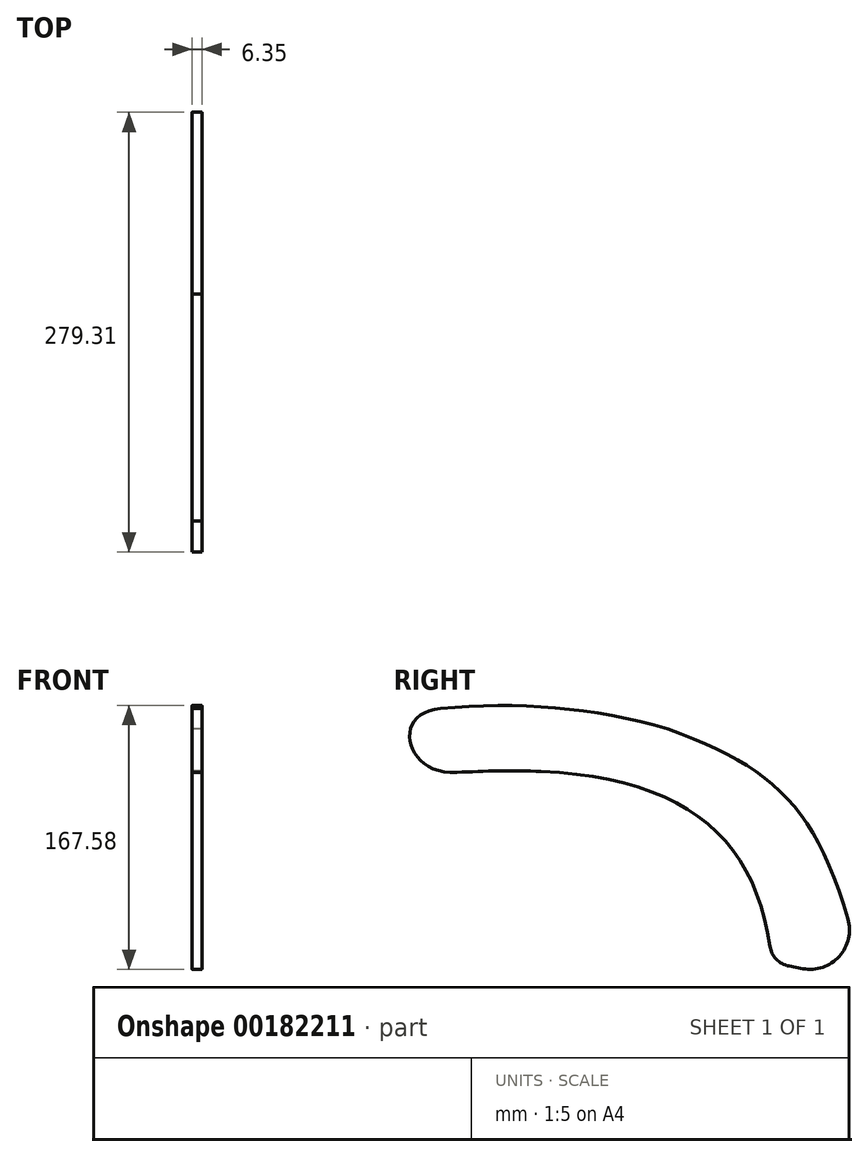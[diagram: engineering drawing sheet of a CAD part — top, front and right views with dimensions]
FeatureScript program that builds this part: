
annotation { "Feature Type Name" : "Feature", "Feature Type Description" : "" }
export const myFeature = defineFeature(function(context is Context, id is Id, definition is map)
    precondition{}
    {
        {
            var Q0;
            Q0=qCreatedBy(makeId("Right.planeOp"),FACE);
            var sketch = newSketch(context, id + "F0", { "sketchPlane" : qUnion([Q0])});
            skFitSpline(sketch, "E0", {"points": [v(0, 0) * mm, v(192, -41) * mm], "startDerivative": vector(239.03, 12.63) * mm, "endDerivative": vector(177.27, -126.97) * mm, "construction": true});
            skArc(sketch, "E1.0.startCap", {"start": v(0.4, -7.49) * mm, "mid": v(-7.49, -0.4) * mm, "end": v(-0.4, 7.49) * mm});
            skArc(sketch, "E1.0.endCap", {"start": v(196.37, -34.9) * mm, "mid": v(198.1, -45.37) * mm, "end": v(187.63, -47.1) * mm});
            skFitSpline(sketch, "E1.0.left", {"points": [v(-0.38, 7.24) * mm, v(19.62, 8.3) * mm, v(47.27, 9.22) * mm, v(81.02, 7.57) * mm, v(105.14, 4.47) * mm, v(128.41, -0.91) * mm, v(151.15, -8.97) * mm, v(173.62, -20.05) * mm, v(188.64, -29.68) * mm, v(196.22, -35.1) * mm]});
            skFitSpline(sketch, "E1.0.right", {"points": [v(0.38, -7.24) * mm, v(20.22, -6.2) * mm, v(47.37, -5.3) * mm, v(79.8, -6.9) * mm, v(102.62, -9.84) * mm, v(124.36, -14.87) * mm, v(145.48, -22.35) * mm, v(166.43, -32.67) * mm, v(180.59, -41.74) * mm, v(187.78, -46.9) * mm]});
            skLineSegment(sketch, "E2", {"start": v(229.1, -144.67) * mm, "end": v(220.28, -143.03) * mm});
            skFitSpline(sketch, "E3", {"points": [v(209.4, -141) * mm, v(62.86, -19.41) * mm], "startDerivative": vector(-20.35, 227.9) * mm, "endDerivative": vector(-284.66, 11.89) * mm});
            skFitSpline(sketch, "E4", {"points": [v(143.32, 7.74) * mm, v(267.73, -151.85) * mm], "startDerivative": vector(228.79, -86.1) * mm, "endDerivative": vector(73.25, -316.4) * mm});
            skArc(sketch, "E5.filletArc", {"start": v(208.17, -130.4) * mm, "mid": v(212.2, -138.66) * mm, "end": v(220.28, -143.03) * mm});
            skArc(sketch, "E6.filletArc", {"start": v(229.1, -144.67) * mm, "mid": v(252.25, -136.83) * mm, "end": v(257.65, -113) * mm});
            skFitSpline(sketch, "E7", {"points": [v(9.37, -20.06) * mm, v(-1.08, 20.47) * mm], "startDerivative": vector(-100.53, -5.96) * mm, "endDerivative": vector(93.66, 6.16) * mm});
            skFitSpline(sketch, "E8", {"points": [v(1.08, -20.47) * mm, v(10.92, -19.95) * mm, v(29.66, -19.14) * mm, v(55.26, -18.95) * mm, v(78.69, -20.11) * mm, v(100.33, -22.91) * mm, v(120.66, -27.62) * mm, v(140.3, -34.58) * mm, v(159.86, -44.21) * mm, v(173.22, -52.77) * mm, v(180.06, -57.67) * mm], "construction": true});
            skArc(sketch, "E9", {"start": v(143.32, 7.74) * mm, "mid": v(71.73, 21) * mm, "end": v(-1.08, 20.47) * mm});
            skArc(sketch, "E10", {"start": v(62.86, -19.41) * mm, "mid": v(36.1, -19.12) * mm, "end": v(9.37, -20.06) * mm});
            skSolve(sketch);
        }
        {
            var Q0;
            Q0 = qSketchRegion(id + "F0", true);
            extrude(context, id + "F1", {"entities" : qUnion([Q0]), "depth" : 6.35 * mm});
        }
    });
